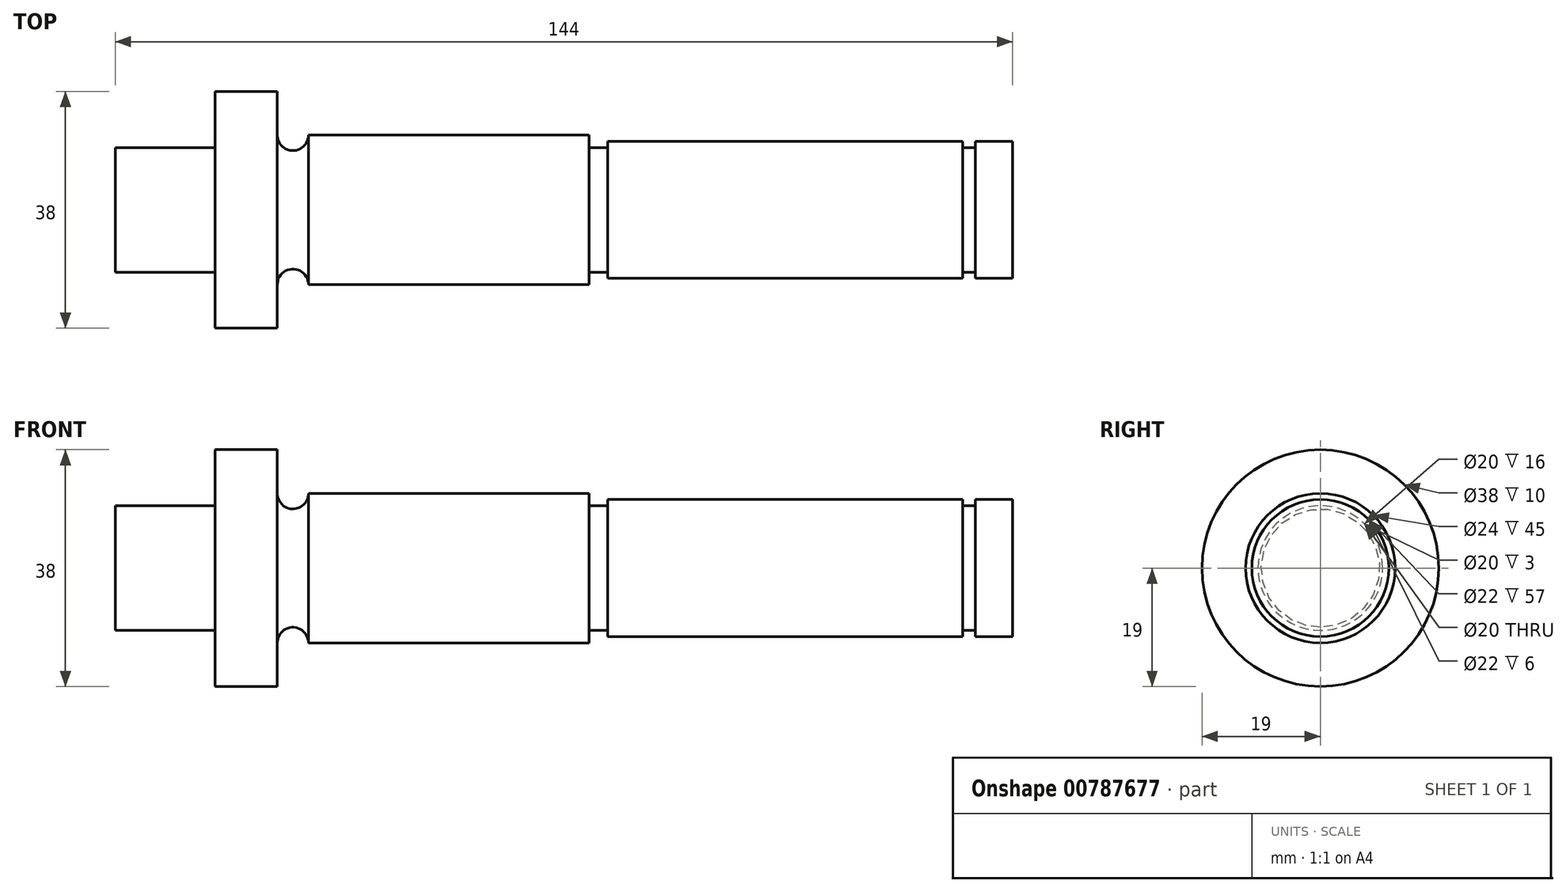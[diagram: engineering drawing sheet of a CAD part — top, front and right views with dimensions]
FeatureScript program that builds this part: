
annotation { "Feature Type Name" : "Feature", "Feature Type Description" : "" }
export const myFeature = defineFeature(function(context is Context, id is Id, definition is map)
    precondition{}
    {
        {
            var Q0;
            Q0=qCreatedBy(makeId("Front.planeOp"),FACE);
            var sketch = newSketch(context, id + "F0", { "sketchPlane" : qUnion([Q0])});
            skLineSegment(sketch, "E0", {"start": v(0, 0) * mm, "end": v(144, 0) * mm});
            skLineSegment(sketch, "E1", {"start": v(0, 0) * mm, "end": v(0, 10) * mm});
            skLineSegment(sketch, "E2", {"start": v(0, 10) * mm, "end": v(16, 10) * mm});
            skLineSegment(sketch, "E3", {"start": v(16, 10) * mm, "end": v(16, 19) * mm});
            skLineSegment(sketch, "E4", {"start": v(16, 19) * mm, "end": v(26, 19) * mm});
            skLineSegment(sketch, "E5", {"start": v(26, 19) * mm, "end": v(26, 12) * mm});
            skLineSegment(sketch, "E6", {"start": v(76, 12) * mm, "end": v(76, 10) * mm});
            skLineSegment(sketch, "E7", {"start": v(76, 10) * mm, "end": v(79, 10) * mm});
            skLineSegment(sketch, "E8", {"start": v(79, 10) * mm, "end": v(79, 11) * mm});
            skLineSegment(sketch, "E9", {"start": v(79, 11) * mm, "end": v(136, 11) * mm});
            skLineSegment(sketch, "E10", {"start": v(136, 11) * mm, "end": v(136, 10) * mm});
            skLineSegment(sketch, "E11", {"start": v(136, 10) * mm, "end": v(138, 10) * mm});
            skLineSegment(sketch, "E12", {"start": v(138, 10) * mm, "end": v(138, 11) * mm});
            skLineSegment(sketch, "E13", {"start": v(138, 11) * mm, "end": v(144, 11) * mm});
            skLineSegment(sketch, "E14", {"start": v(144, 11) * mm, "end": v(144, 0) * mm});
            skArc(sketch, "E15", {"start": v(26, 12) * mm, "mid": v(28.5, 9.5) * mm, "end": v(31, 12) * mm});
            skLineSegment(sketch, "E16", {"start": v(31, 12) * mm, "end": v(76, 12) * mm});
            skSolve(sketch);
        }
        {
            var Q0;
            Q0=sQuery(id+"F0.wireOp",EDGE,"E1");
            var Q1;
            Q1=sQuery(id+"F0.wireOp",EDGE,"E2");
            var Q2;
            Q2=sQuery(id+"F0.wireOp",EDGE,"E4");
            var Q3;
            Q3=sQuery(id+"F0.wireOp",EDGE,"E3");
            var Q4;
            Q4=sQuery(id+"F0.wireOp",EDGE,"E5");
            var Q5;
            Q5=sQuery(id+"F0.wireOp",EDGE,"E15");
            var Q6;
            Q6=sQuery(id+"F0.wireOp",EDGE,"E16");
            var Q7;
            Q7=sQuery(id+"F0.wireOp",EDGE,"E6");
            var Q8;
            Q8=sQuery(id+"F0.wireOp",EDGE,"E7");
            var Q9;
            Q9=sQuery(id+"F0.wireOp",EDGE,"E8");
            var Q10;
            Q10=sQuery(id+"F0.wireOp",EDGE,"E9");
            var Q11;
            Q11=sQuery(id+"F0.wireOp",EDGE,"E14");
            var Q12;
            Q12=sQuery(id+"F0.wireOp",EDGE,"E13");
            var Q13;
            Q13=sQuery(id+"F0.wireOp",EDGE,"E11");
            var Q14;
            Q14=sQuery(id+"F0.wireOp",EDGE,"E0");
            revolve(context, id + "F1", {"bodyType" : ToolBodyType.SURFACE, "surfaceOperationType" : NewSurfaceOperationType.NEW, "surfaceEntities" : qUnion([Q0, Q1, Q2, Q3, Q4, Q5, Q6, Q7, Q8, Q9, Q10, Q11, Q12, Q13]), "axis" : qUnion([Q14]), "revolveType" : RevolveType.FULL});
        }
    });
